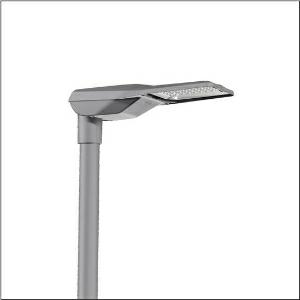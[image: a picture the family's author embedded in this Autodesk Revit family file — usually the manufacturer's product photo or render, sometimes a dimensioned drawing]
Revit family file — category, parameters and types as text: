
# Revit family: streetlight_sl_21_iq_mini___st1_0ab_5xe2m31d08gb_7ae7
name_source: partatom
category: Lighting Fixtures
units: mm (PartAtom-declared; Revit-internal decimal feet)

## family parameters
Cut with Voids When Loaded = No
Host = Face
Light Source = No
Part Type = Normal
Room Calculation Point = No
Round Connector Dimension = Use Diameter
Shared = No

## types (1)
- --- (1 x LED, 5000 lm, 37.1 W, 3000K)
    Apparent Load = 37 VA
    CIE Flux Codes = 38 73 97 100 100
    Color Rendering = 70
    Color Temperature = 3000K
    Default Elevation = 1800 mm
    Description = Streetlight SL 21 iQ mini, mast luminaire, primary light control with lens, of PMMA, primary optical cover: cover, of toughened safety glass, transparent, light distribution: ST1.0aB, light emission: direct distribution, primary light characteristic: asymmetric, installation type: post-top, side-entry, LED, High Power LED, rated luminous flux: 5.000lm, luminous efficacy: 135lm/W, light colour: 730, colour temperature: 3000K, control gear: iQ-Comfort, control: Auto-Match, Temp-Guard, Lumen-Switch, Night-Set, Smart-Wire, Light-Fading, Desk-Remote (wireless, voltage-free reading and setting of iQ features in the workshop via application-optimized NFC function/RFID function), optimised constant luminous flux control (CLO 2.0), pre-setting: linear dimming characteristic, mains connection: 220..240V, AC, 50/60Hz, start of lifetime: 37W, end of service life: 39W, reduction: 18W, luminaire housing, of diecast aluminium, powder-coated, SITECO metallic grey (DB 702S), corrosivity category C5 high according to DIN EN ISO 12944, please order mast flange separately, inclination adjustable: 0°, 5°, 10°, 15°, sealing non-destructively replaceable, multi-level sealing system, length: 628mm, width: 235mm, height: 110mm, mast flange for spigot size: 42mm (side-entry): 5XC10008XM4, 60/48mm (side-entry/post-top): 5XC10108XM2, 76/60mm (side-entry/post-top): 5XC10108XM1, mounting height: 4..8m, protection rating (complete): IP66, insulation class (complete): insulation class II (safety insulation), certification: CE, ENEC, ENEC+, VDE, impact resistance: IK10, permissible operating ambient temperature for outdoor applications: -40..+50°C, standard-compliant lighting for roads and squares, packaging unit: 1 piece

Light Distribution: ST1.0aB
    Height = 110 mm
    Lamp = 1 x LED
    Lamp Light Flux = 5000 lm
    Lamp Power = 37.1 W
    Lamp count = 1
    Length = 625 mm
    Luminous efficacy = 135 lm/W
    Manufacturer = Siteco
    ModVariant = No
    Model = 5XE2M31D08GB
    Number of Poles = 1
    OnlyDefault = Yes
    Power Factor = 1
    Product Name = Streetlight SL 21 iQ mini | ST1.0aB
    Product group = mast luminaire | pylon top
    ProductGroupID = 6100
    Protection Class = Protection class II
    Protection Degree = IP 66
    RLX_Detail_Level = 1
    RLX_Emergency_Light_Flux = 0 lm
    RLX_Emergency_Type = 0
    RLX_Emergency_Type_DB = No
    RlxData = <blob elided: 26321 chars, md5=55a17160>
    Socket = socket
    Standby Power = 0 W
    System Light Flux = 5000 lm
    System Power = 37 W
    Type Comments = factory setting: luminous flux: 100 % | dim-lin: 254 | 385 mA
    Type Image = l_1003519.jpg
    URL = http://relux.com
    VarID = @adj_180231
    Voltage = 0 V
    Weight = 0.00 kg
    Width = 234 mm

## geometry (parser evidence)
native form markers: Blend x4, Sweep x9
no freeform markers — native parametric forms only
